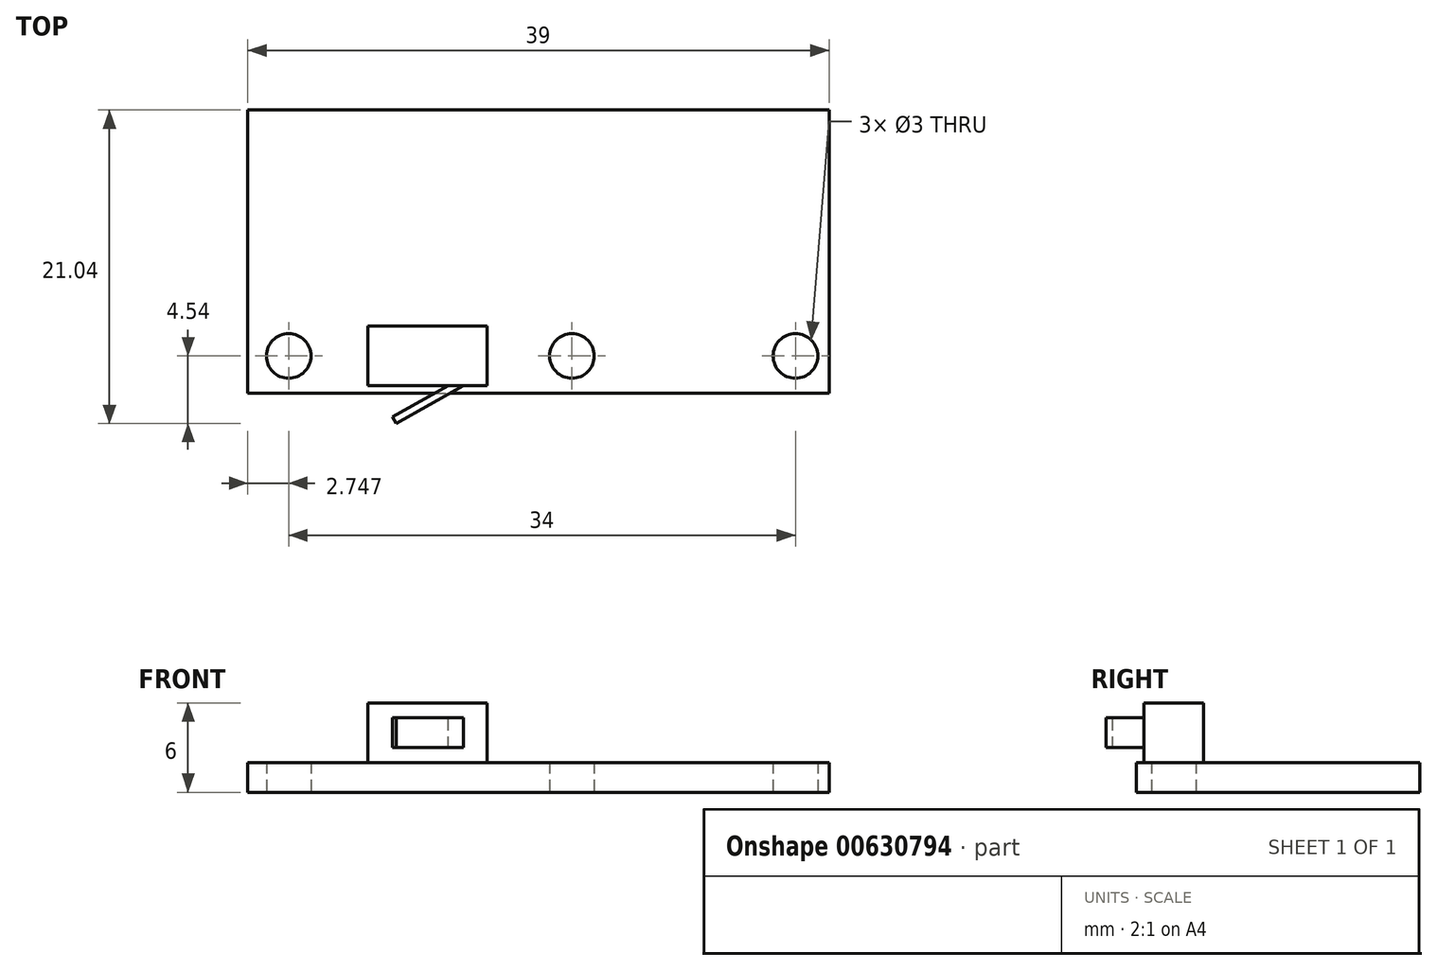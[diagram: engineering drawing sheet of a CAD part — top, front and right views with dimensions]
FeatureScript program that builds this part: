
annotation { "Feature Type Name" : "Feature", "Feature Type Description" : "" }
export const myFeature = defineFeature(function(context is Context, id is Id, definition is map)
    precondition{}
    {
        {
            var Q0;
            Q0=qCreatedBy(makeId("Top.planeOp"),FACE);
            var sketch = newSketch(context, id + "F0", { "sketchPlane" : qUnion([Q0])});
            skLineSegment(sketch, "E0.bottom", {"start": v(0, 0) * mm, "end": v(39, 0) * mm});
            skLineSegment(sketch, "E0.top", {"start": v(0, 19) * mm, "end": v(39, 19) * mm});
            skLineSegment(sketch, "E0.left", {"start": v(0, 0) * mm, "end": v(0, 19) * mm});
            skLineSegment(sketch, "E0.right", {"start": v(39, 0) * mm, "end": v(39, 19) * mm});
            skCircle(sketch, "E1", {"center": v(2.75, 2.5) * mm, "radius": 1.5 * mm});
            skCircle(sketch, "E2", {"center": v(21.75, 2.5) * mm, "radius": 1.5 * mm});
            skCircle(sketch, "E3", {"center": v(36.75, 2.5) * mm, "radius": 1.5 * mm});
            skSolve(sketch);
        }
        {
            var Q0;
            Q0=makeQuery(id+"F0.imprint","IMPRINT",FACE,{"disambiguationData":[TD([[makeQuery(id+"F0.imprint","IMPRINT",EDGE,{"derivedFrom":sQuery(id+"F0.wireOp",EDGE,"E0.bottom")}),1.0]])]});
            extrude(context, id + "F1", {"entities" : qUnion([Q0]), "depth" : 2 * mm, "offsetDistance" : 25 * mm});
        }
        {
            var Q0;
            Q0=makeQuery(id+"F1.opExtrude","CAP_FACE",FACE,{"disambiguationData":[OSD([sQuery(id+"F0.wireOp",EDGE,"E0.bottom"),sQuery(id+"F0.wireOp",EDGE,"E0.top"),sQuery(id+"F0.wireOp",EDGE,"E0.left"),sQuery(id+"F0.wireOp",EDGE,"E0.right"),sQuery(id+"F0.wireOp",EDGE,"E1"),sQuery(id+"F0.wireOp",EDGE,"E2"),sQuery(id+"F0.wireOp",EDGE,"E3")])],"isStart":false});
            var sketch = newSketch(context, id + "F2", { "sketchPlane" : qUnion([Q0])});
            skLineSegment(sketch, "E4.bottom", {"start": v(8.05, 4.5) * mm, "end": v(16.05, 4.5) * mm});
            skLineSegment(sketch, "E4.top", {"start": v(8.05, 0.5) * mm, "end": v(16.05, 0.5) * mm});
            skLineSegment(sketch, "E4.left", {"start": v(8.05, 4.5) * mm, "end": v(8.05, 0.5) * mm});
            skLineSegment(sketch, "E4.right", {"start": v(16.05, 4.5) * mm, "end": v(16.05, 0.5) * mm});
            skSolve(sketch);
        }
        {
            var Q0;
            Q0=makeQuery(id+"F2.imprint","IMPRINT",FACE,{"disambiguationData":[TD([[makeQuery(id+"F2.imprint","IMPRINT",EDGE,{"derivedFrom":sQuery(id+"F2.wireOp",EDGE,"E4.bottom")}),-1.0]])]});
            extrude(context, id + "F3", {"entities" : qUnion([Q0]), "operationType" : NewBodyOperationType.ADD, "depth" : 4 * mm, "offsetDistance" : 25 * mm});
        }
        {
            var Q0;
            Q0=makeQuery(id+"FxsfhzeGUpP34Ln_1.imprint","IMPRINT",FACE,{"disambiguationData":[TD([[makeQuery(id+"FxsfhzeGUpP34Ln_1.imprint","IMPRINT",EDGE,{"derivedFrom":makeQuery(id+"F3.opExtrude","CAP_EDGE",EDGE,{"disambiguationData":[OSD([sQuery(id+"F2.wireOp",EDGE,"E4.bottom")])],"isStart":false})}),-1.0]])]});
            var Q1;
            Q1=makeQuery(id+"F3.opExtrude","CAP_FACE",FACE,{"disambiguationData":[OSD([sQuery(id+"F2.wireOp",EDGE,"E4.bottom"),sQuery(id+"F2.wireOp",EDGE,"E4.top"),sQuery(id+"F2.wireOp",EDGE,"E4.left"),sQuery(id+"F2.wireOp",EDGE,"E4.right")])],"isStart":false});
            cPlane(context, id + "F4", {"entities" : qUnion([Q0, Q1]), "cplaneType" : CPlaneType.OFFSET, "offset" : 1 * mm, "oppositeDirection" : true, "width" : 150 * mm, "height" : 150 * mm});
        }
        {
            var Q0;
            Q0=qCreatedBy(id+"F4.planeOp",FACE);
            var sketch = newSketch(context, id + "F5", { "sketchPlane" : qUnion([Q0])});
            skLineSegment(sketch, "E5", {"start": v(14.94, 1.35) * mm, "end": v(9.72, -1.6) * mm});
            skLineSegment(sketch, "E6", {"start": v(9.72, -1.6) * mm, "end": v(9.97, -2.04) * mm});
            skLineSegment(sketch, "E7", {"start": v(9.97, -2.04) * mm, "end": v(15.2, 0.92) * mm});
            skLineSegment(sketch, "E8", {"start": v(15.2, 0.92) * mm, "end": v(14.94, 1.35) * mm});
            skSolve(sketch);
        }
        {
            var Q0;
            Q0=makeQuery(id+"F5.imprint","IMPRINT",FACE,{"disambiguationData":[TD([[makeQuery(id+"F5.imprint","IMPRINT",EDGE,{"derivedFrom":sQuery(id+"F5.wireOp",EDGE,"E5")}),1.0]])]});
            extrude(context, id + "F6", {"entities" : qUnion([Q0]), "operationType" : NewBodyOperationType.ADD, "oppositeDirection" : true, "depth" : 2 * mm, "offsetDistance" : 25 * mm});
        }
    });
